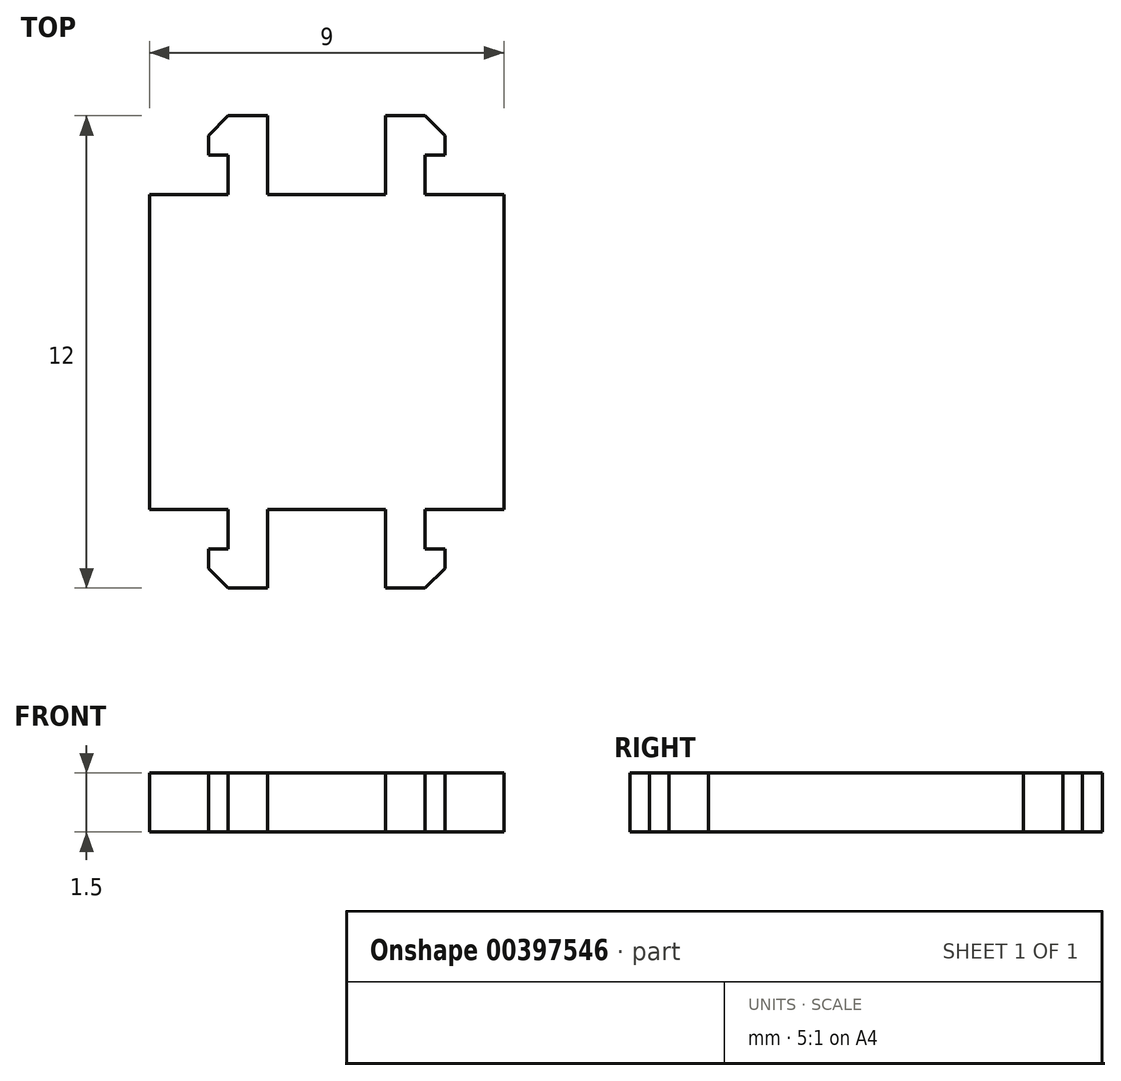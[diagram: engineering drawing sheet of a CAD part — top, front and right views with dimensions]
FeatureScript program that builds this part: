
annotation { "Feature Type Name" : "Feature", "Feature Type Description" : "" }
export const myFeature = defineFeature(function(context is Context, id is Id, definition is map)
    precondition{}
    {
        {
            var Q0;
            Q0=qCreatedBy(makeId("Top.planeOp"),FACE);
            var sketch = newSketch(context, id + "F0", { "sketchPlane" : qUnion([Q0])});
            skLineSegment(sketch, "E0.bottom", {"start": v(4.5, 4) * mm, "end": v(-4.5, 4) * mm});
            skLineSegment(sketch, "E0.top", {"start": v(4.5, -4) * mm, "end": v(-4.5, -4) * mm});
            skLineSegment(sketch, "E0.left", {"start": v(4.5, 4) * mm, "end": v(4.5, -4) * mm});
            skLineSegment(sketch, "E0.right", {"start": v(-4.5, 4) * mm, "end": v(-4.5, -4) * mm});
            skPoint(sketch, "E0.middle", {"position": v(0, 0) * mm});
            skLineSegment(sketch, "E1.bottom", {"start": v(2.5, 6) * mm, "end": v(-2.5, 6) * mm});
            skLineSegment(sketch, "E1.top", {"start": v(2.5, -6) * mm, "end": v(-2.5, -6) * mm});
            skLineSegment(sketch, "E1.left", {"start": v(2.5, 6) * mm, "end": v(2.5, -6) * mm});
            skLineSegment(sketch, "E1.right", {"start": v(-2.5, 6) * mm, "end": v(-2.5, -6) * mm});
            skLineSegment(sketch, "E2.bottom", {"start": v(1.5, -6) * mm, "end": v(-1.5, -6) * mm});
            skLineSegment(sketch, "E2.top", {"start": v(1.5, 6) * mm, "end": v(-1.5, 6) * mm});
            skLineSegment(sketch, "E2.left", {"start": v(1.5, -6) * mm, "end": v(1.5, 6) * mm});
            skLineSegment(sketch, "E2.right", {"start": v(-1.5, -6) * mm, "end": v(-1.5, 6) * mm});
            skLineSegment(sketch, "E3.bottom", {"start": v(-3, 6) * mm, "end": v(3, 6) * mm});
            skLineSegment(sketch, "E3.top", {"start": v(-3, 5) * mm, "end": v(3, 5) * mm});
            skLineSegment(sketch, "E3.left", {"start": v(-3, 6) * mm, "end": v(-3, 5) * mm});
            skLineSegment(sketch, "E3.right", {"start": v(3, 6) * mm, "end": v(3, 5) * mm});
            skPoint(sketch, "E4", {"position": v(0, 6) * mm});
            skLineSegment(sketch, "E5.MirrorCS", {"start": v(-3, -6) * mm, "end": v(-3, -5) * mm});
            skLineSegment(sketch, "E6.MirrorCS", {"start": v(3, -6) * mm, "end": v(3, -5) * mm});
            skPoint(sketch, "E7.MirrorP", {"position": v(0, -6) * mm});
            skLineSegment(sketch, "E8.MirrorCS", {"start": v(-3, -6) * mm, "end": v(3, -6) * mm});
            skLineSegment(sketch, "E9.MirrorCS", {"start": v(-3, -5) * mm, "end": v(3, -5) * mm});
            skSolve(sketch);
        }
        {
            var Q0;
            {var subQ0=sQuery(id+"F0.wireOp",EDGE,"E1.right");var subQ1=sQuery(id+"F0.wireOp",EDGE,"E0.bottom");var subQ2=makeQuery(id+"F0.imprint","INTERSECT",VERTEX,{"derivedFrom":[subQ1,subQ0]});Q0=makeQuery(id+"F0.imprint","IMPRINT",FACE,{"disambiguationData":[TD([[makeQuery(id+"F0.imprint","IMPRINT",EDGE,{"disambiguationData":[TD([[subQ2,1.0]])],"derivedFrom":subQ1}),-1.0]])]});}
            var Q1;
            {var subQ0=sQuery(id+"F0.wireOp",EDGE,"E1.left");var subQ1=sQuery(id+"F0.wireOp",EDGE,"E0.bottom");var subQ2=makeQuery(id+"F0.imprint","INTERSECT",VERTEX,{"derivedFrom":[subQ1,subQ0]});Q1=makeQuery(id+"F0.imprint","IMPRINT",FACE,{"disambiguationData":[TD([[makeQuery(id+"F0.imprint","IMPRINT",EDGE,{"disambiguationData":[TD([[subQ2,-1.0]])],"derivedFrom":subQ1}),-1.0]])]});}
            var Q2;
            {var subQ0=sQuery(id+"F0.wireOp",EDGE,"E0.left");Q2=makeQuery(id+"F0.imprint","IMPRINT",FACE,{"disambiguationData":[TD([[makeQuery(id+"F0.imprint","IMPRINT",EDGE,{"derivedFrom":subQ0}),-1.0]])]});}
            var Q3;
            {var subQ0=sQuery(id+"F0.wireOp",EDGE,"E1.left");var subQ1=sQuery(id+"F0.wireOp",EDGE,"E0.bottom");var subQ2=makeQuery(id+"F0.imprint","INTERSECT",VERTEX,{"derivedFrom":[subQ1,subQ0]});Q3=makeQuery(id+"F0.imprint","IMPRINT",FACE,{"disambiguationData":[TD([[makeQuery(id+"F0.imprint","IMPRINT",EDGE,{"disambiguationData":[TD([[subQ2,-1.0]])],"derivedFrom":subQ1}),1.0]])]});}
            var Q4;
            {var subQ0=sQuery(id+"F0.wireOp",EDGE,"E2.left");var subQ1=sQuery(id+"F0.wireOp",EDGE,"E0.bottom");var subQ2=makeQuery(id+"F0.imprint","INTERSECT",VERTEX,{"derivedFrom":[subQ1,subQ0]});Q4=makeQuery(id+"F0.imprint","IMPRINT",FACE,{"disambiguationData":[TD([[makeQuery(id+"F0.imprint","IMPRINT",EDGE,{"disambiguationData":[TD([[subQ2,-1.0]])],"derivedFrom":subQ1}),1.0]])]});}
            var Q5;
            {var subQ0=sQuery(id+"F0.wireOp",EDGE,"E1.right");var subQ1=sQuery(id+"F0.wireOp",EDGE,"E0.bottom");var subQ2=makeQuery(id+"F0.imprint","INTERSECT",VERTEX,{"derivedFrom":[subQ1,subQ0]});Q5=makeQuery(id+"F0.imprint","IMPRINT",FACE,{"disambiguationData":[TD([[makeQuery(id+"F0.imprint","IMPRINT",EDGE,{"disambiguationData":[TD([[subQ2,1.0]])],"derivedFrom":subQ1}),1.0]])]});}
            var Q6;
            {var subQ0=sQuery(id+"F0.wireOp",EDGE,"E0.right");Q6=makeQuery(id+"F0.imprint","IMPRINT",FACE,{"disambiguationData":[TD([[makeQuery(id+"F0.imprint","IMPRINT",EDGE,{"derivedFrom":subQ0}),1.0]])]});}
            var Q7;
            {var subQ0=sQuery(id+"F0.wireOp",EDGE,"E1.right");var subQ1=sQuery(id+"F0.wireOp",EDGE,"E0.top");var subQ2=makeQuery(id+"F0.imprint","INTERSECT",VERTEX,{"derivedFrom":[subQ1,subQ0]});Q7=makeQuery(id+"F0.imprint","IMPRINT",FACE,{"disambiguationData":[TD([[makeQuery(id+"F0.imprint","IMPRINT",EDGE,{"disambiguationData":[TD([[subQ2,1.0]])],"derivedFrom":subQ1}),1.0]])]});}
            var Q8;
            {var subQ0=sQuery(id+"F0.wireOp",EDGE,"E1.left");var subQ1=sQuery(id+"F0.wireOp",EDGE,"E0.top");var subQ2=makeQuery(id+"F0.imprint","INTERSECT",VERTEX,{"derivedFrom":[subQ1,subQ0]});Q8=makeQuery(id+"F0.imprint","IMPRINT",FACE,{"disambiguationData":[TD([[makeQuery(id+"F0.imprint","IMPRINT",EDGE,{"disambiguationData":[TD([[subQ2,-1.0]])],"derivedFrom":subQ1}),1.0]])]});}
            var Q9;
            {var subQ5=sQuery(id+"F0.wireOp",EDGE,"E3.left");Q9=makeQuery(id+"F0.imprint","IMPRINT",FACE,{"disambiguationData":[TD([[makeQuery(id+"F0.imprint","IMPRINT",EDGE,{"derivedFrom":subQ5}),1.0]])]});}
            var Q10;
            {var subQ0=sQuery(id+"F0.wireOp",EDGE,"E3.bottom");var subQ1=sQuery(id+"F0.wireOp",EDGE,"E1.right");var subQ2=makeQuery(id+"F0.imprint","INTERSECT",VERTEX,{"derivedFrom":[subQ1,subQ0]});Q10=makeQuery(id+"F0.imprint","IMPRINT",FACE,{"disambiguationData":[TD([[makeQuery(id+"F0.imprint","IMPRINT",EDGE,{"disambiguationData":[TD([[subQ2,-1.0]])],"derivedFrom":subQ1}),1.0]])]});}
            var Q11;
            {var subQ0=sQuery(id+"F0.wireOp",EDGE,"E3.bottom");var subQ1=sQuery(id+"F0.wireOp",EDGE,"E1.left");var subQ2=makeQuery(id+"F0.imprint","INTERSECT",VERTEX,{"derivedFrom":[subQ1,subQ0]});Q11=makeQuery(id+"F0.imprint","IMPRINT",FACE,{"disambiguationData":[TD([[makeQuery(id+"F0.imprint","IMPRINT",EDGE,{"disambiguationData":[TD([[subQ2,-1.0]])],"derivedFrom":subQ1}),-1.0]])]});}
            var Q12;
            {var subQ5=sQuery(id+"F0.wireOp",EDGE,"E3.right");Q12=makeQuery(id+"F0.imprint","IMPRINT",FACE,{"disambiguationData":[TD([[makeQuery(id+"F0.imprint","IMPRINT",EDGE,{"derivedFrom":subQ5}),-1.0]])]});}
            var Q13;
            {var subQ0=sQuery(id+"F0.wireOp",EDGE,"E8.MirrorCS");var subQ1=sQuery(id+"F0.wireOp",EDGE,"E1.left");var subQ2=makeQuery(id+"F0.imprint","INTERSECT",VERTEX,{"derivedFrom":[subQ1,subQ0]});Q13=makeQuery(id+"F0.imprint","IMPRINT",FACE,{"disambiguationData":[TD([[makeQuery(id+"F0.imprint","IMPRINT",EDGE,{"disambiguationData":[TD([[subQ2,1.0]])],"derivedFrom":subQ1}),-1.0]])]});}
            var Q14;
            {var subQ5=sQuery(id+"F0.wireOp",EDGE,"E6.MirrorCS");Q14=makeQuery(id+"F0.imprint","IMPRINT",FACE,{"disambiguationData":[TD([[makeQuery(id+"F0.imprint","IMPRINT",EDGE,{"derivedFrom":subQ5}),1.0]])]});}
            var Q15;
            {var subQ5=sQuery(id+"F0.wireOp",EDGE,"E5.MirrorCS");Q15=makeQuery(id+"F0.imprint","IMPRINT",FACE,{"disambiguationData":[TD([[makeQuery(id+"F0.imprint","IMPRINT",EDGE,{"derivedFrom":subQ5}),-1.0]])]});}
            var Q16;
            {var subQ0=sQuery(id+"F0.wireOp",EDGE,"E8.MirrorCS");var subQ1=sQuery(id+"F0.wireOp",EDGE,"E1.right");var subQ2=makeQuery(id+"F0.imprint","INTERSECT",VERTEX,{"derivedFrom":[subQ1,subQ0]});Q16=makeQuery(id+"F0.imprint","IMPRINT",FACE,{"disambiguationData":[TD([[makeQuery(id+"F0.imprint","IMPRINT",EDGE,{"disambiguationData":[TD([[subQ2,1.0]])],"derivedFrom":subQ1}),1.0]])]});}
            extrude(context, id + "F1", {"entities" : qUnion([Q0, Q1, Q2, Q3, Q4, Q5, Q6, Q7, Q8, Q9, Q10, Q11, Q12, Q13, Q14, Q15, Q16]), "depth" : 1.5 * mm});
        }
        {
            var Q0;
            Q0=makeQuery(id+"F1.opExtrude","SWEPT_EDGE",EDGE,{"disambiguationData":[OSD([sQuery(id+"F0.wireOp",EDGE,"E3.bottom"),sQuery(id+"F0.wireOp",EDGE,"E3.left")])]});
            var Q1;
            Q1=makeQuery(id+"F1.opExtrude","SWEPT_EDGE",EDGE,{"disambiguationData":[OSD([sQuery(id+"F0.wireOp",EDGE,"E3.bottom"),sQuery(id+"F0.wireOp",EDGE,"E3.right")])]});
            var Q2;
            Q2=makeQuery(id+"F1.opExtrude","SWEPT_EDGE",EDGE,{"disambiguationData":[OSD([sQuery(id+"F0.wireOp",EDGE,"E6.MirrorCS"),sQuery(id+"F0.wireOp",EDGE,"E8.MirrorCS")])]});
            var Q3;
            Q3=makeQuery(id+"F1.opExtrude","SWEPT_EDGE",EDGE,{"disambiguationData":[OSD([sQuery(id+"F0.wireOp",EDGE,"E5.MirrorCS"),sQuery(id+"F0.wireOp",EDGE,"E8.MirrorCS")])]});
            chamfer(context, id + "F2", {"entities" : qUnion([Q0, Q1, Q2, Q3]), "width" : 0.5 * mm, "tangentPropagation" : true});
        }
    });
